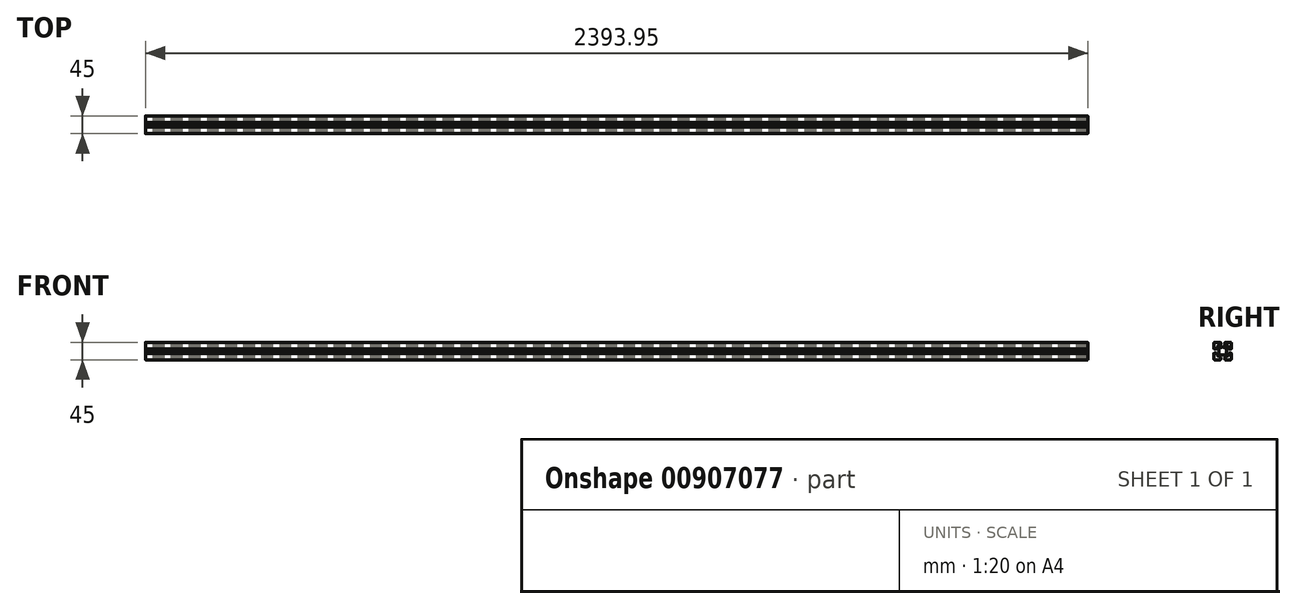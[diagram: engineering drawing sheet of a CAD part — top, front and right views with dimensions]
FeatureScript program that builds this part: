
annotation { "Feature Type Name" : "Feature", "Feature Type Description" : "" }
export const myFeature = defineFeature(function(context is Context, id is Id, definition is map)
    precondition{}
    {
        {
            var Q0;
            Q0=qCreatedBy(makeId("Right.planeOp"),FACE);
            var sketch = newSketch(context, id + "F0", { "sketchPlane" : qUnion([Q0])});
            skLineSegment(sketch, "E0", {"start": v(-20.09, -10.29) * mm, "end": v(-21.29, -10.29) * mm});
            skArc(sketch, "E1", {"start": v(-21.29, -10.29) * mm, "mid": v(-21.5, -10.38) * mm, "end": v(-21.59, -10.59) * mm});
            skLineSegment(sketch, "E2", {"start": v(-21.59, -10.59) * mm, "end": v(-21.59, -23.99) * mm});
            skArc(sketch, "E3", {"start": v(-21.59, -23.99) * mm, "mid": v(-20.7, -26.11) * mm, "end": v(-18.59, -26.99) * mm});
            skLineSegment(sketch, "E4", {"start": v(-18.59, -26.99) * mm, "end": v(-5.19, -26.99) * mm});
            skArc(sketch, "E5", {"start": v(-5.19, -26.99) * mm, "mid": v(-4.98, -26.9) * mm, "end": v(-4.89, -26.69) * mm});
            skLineSegment(sketch, "E6", {"start": v(-4.89, -26.69) * mm, "end": v(-4.89, -25.49) * mm});
            skLineSegment(sketch, "E7", {"start": v(-4.89, -25.49) * mm, "end": v(-4.39, -25.49) * mm});
            skArc(sketch, "E8", {"start": v(-4.39, -25.49) * mm, "mid": v(-4.18, -25.4) * mm, "end": v(-4.09, -25.19) * mm});
            skLineSegment(sketch, "E9", {"start": v(-4.09, -25.19) * mm, "end": v(-4.09, -21.29) * mm});
            skArc(sketch, "E10", {"start": v(-4.09, -21.29) * mm, "mid": v(-4.18, -21.08) * mm, "end": v(-4.39, -20.99) * mm});
            skLineSegment(sketch, "E11", {"start": v(-4.39, -20.99) * mm, "end": v(-9.14, -20.99) * mm});
            skLineSegment(sketch, "E12", {"start": v(-9.14, -20.99) * mm, "end": v(-9.14, -16.88) * mm});
            skLineSegment(sketch, "E13", {"start": v(-9.14, -16.88) * mm, "end": v(-6.25, -13.99) * mm});
            skLineSegment(sketch, "E14", {"start": v(-6.25, -13.99) * mm, "end": v(-2.21, -13.99) * mm});
            skArc(sketch, "E15", {"start": v(-2.21, -13.99) * mm, "mid": v(0.91, -14.49) * mm, "end": v(4.03, -13.99) * mm});
            skLineSegment(sketch, "E16", {"start": v(-20.09, -10.29) * mm, "end": v(-20.09, -9.79) * mm});
            skArc(sketch, "E17", {"start": v(-20.09, -9.79) * mm, "mid": v(-20, -9.58) * mm, "end": v(-19.79, -9.49) * mm});
            skLineSegment(sketch, "E18", {"start": v(-19.79, -9.49) * mm, "end": v(-15.89, -9.49) * mm});
            skArc(sketch, "E19", {"start": v(-15.89, -9.49) * mm, "mid": v(-15.68, -9.58) * mm, "end": v(-15.59, -9.79) * mm});
            skLineSegment(sketch, "E20", {"start": v(-15.59, -9.79) * mm, "end": v(-15.59, -14.54) * mm});
            skLineSegment(sketch, "E21", {"start": v(-15.59, -14.54) * mm, "end": v(-11.48, -14.54) * mm});
            skLineSegment(sketch, "E22", {"start": v(-11.48, -14.54) * mm, "end": v(-8.59, -11.65) * mm});
            skLineSegment(sketch, "E23", {"start": v(-8.59, -11.65) * mm, "end": v(-8.59, -7.61) * mm});
            skLineSegment(sketch, "E24", {"start": v(29.82, -4.49) * mm, "end": v(-31.05, -4.49) * mm});
            skLineSegment(sketch, "E25.MirrorCS", {"start": v(6.71, -25.49) * mm, "end": v(6.21, -25.49) * mm});
            skArc(sketch, "E26.MirrorCS", {"start": v(7.01, -26.99) * mm, "mid": v(6.8, -26.9) * mm, "end": v(6.71, -26.69) * mm});
            skLineSegment(sketch, "E27.MirrorCS", {"start": v(10.41, -11.65) * mm, "end": v(10.41, -7.61) * mm});
            skArc(sketch, "E28.MirrorCS", {"start": v(6.21, -25.49) * mm, "mid": v(6, -25.4) * mm, "end": v(5.91, -25.19) * mm});
            skLineSegment(sketch, "E29.MirrorCS", {"start": v(6.71, -26.69) * mm, "end": v(6.71, -25.49) * mm});
            skArc(sketch, "E30.MirrorCS", {"start": v(5.91, -21.29) * mm, "mid": v(6, -21.08) * mm, "end": v(6.21, -20.99) * mm});
            skLineSegment(sketch, "E31.MirrorCS", {"start": v(10.96, -16.88) * mm, "end": v(8.07, -13.99) * mm});
            skLineSegment(sketch, "E32.MirrorCS", {"start": v(13.3, -14.54) * mm, "end": v(10.41, -11.65) * mm});
            skLineSegment(sketch, "E33.MirrorCS", {"start": v(17.41, -14.54) * mm, "end": v(13.3, -14.54) * mm});
            skLineSegment(sketch, "E34.MirrorCS", {"start": v(17.41, -9.79) * mm, "end": v(17.41, -14.54) * mm});
            skLineSegment(sketch, "E35.MirrorCS", {"start": v(6.21, -20.99) * mm, "end": v(10.96, -20.99) * mm});
            skLineSegment(sketch, "E36.MirrorCS", {"start": v(8.07, -13.99) * mm, "end": v(4.03, -13.99) * mm});
            skArc(sketch, "E37.MirrorCS", {"start": v(4.03, -13.99) * mm, "mid": v(0.91, -14.49) * mm, "end": v(-2.21, -13.99) * mm});
            skLineSegment(sketch, "E38.MirrorCS", {"start": v(10.96, -20.99) * mm, "end": v(10.96, -16.88) * mm});
            skLineSegment(sketch, "E39.MirrorCS", {"start": v(5.91, -25.19) * mm, "end": v(5.91, -21.29) * mm});
            skArc(sketch, "E40.MirrorCS", {"start": v(23.41, -23.99) * mm, "mid": v(22.53, -26.11) * mm, "end": v(20.41, -26.99) * mm});
            skLineSegment(sketch, "E41.MirrorCS", {"start": v(20.41, -26.99) * mm, "end": v(7.01, -26.99) * mm});
            skLineSegment(sketch, "E42.MirrorCS", {"start": v(23.41, -10.59) * mm, "end": v(23.41, -23.99) * mm});
            skArc(sketch, "E43.MirrorCS", {"start": v(17.71, -9.49) * mm, "mid": v(17.5, -9.58) * mm, "end": v(17.41, -9.79) * mm});
            skArc(sketch, "E44.MirrorCS", {"start": v(23.11, -10.29) * mm, "mid": v(23.32, -10.38) * mm, "end": v(23.41, -10.59) * mm});
            skLineSegment(sketch, "E45.MirrorCS", {"start": v(21.91, -10.29) * mm, "end": v(21.91, -9.79) * mm});
            skLineSegment(sketch, "E46.MirrorCS", {"start": v(21.91, -10.29) * mm, "end": v(23.11, -10.29) * mm});
            skArc(sketch, "E47.MirrorCS", {"start": v(21.91, -9.79) * mm, "mid": v(21.82, -9.58) * mm, "end": v(21.61, -9.49) * mm});
            skLineSegment(sketch, "E48.MirrorCS", {"start": v(21.61, -9.49) * mm, "end": v(17.71, -9.49) * mm});
            skLineSegment(sketch, "E49.MirrorCS", {"start": v(6.71, 16.51) * mm, "end": v(6.21, 16.51) * mm});
            skArc(sketch, "E50.MirrorCS", {"start": v(-4.39, 16.51) * mm, "mid": v(-4.18, 16.42) * mm, "end": v(-4.09, 16.21) * mm});
            skLineSegment(sketch, "E51.MirrorCS", {"start": v(-4.89, 16.51) * mm, "end": v(-4.39, 16.51) * mm});
            skArc(sketch, "E52.MirrorCS", {"start": v(5.91, 12.31) * mm, "mid": v(6, 12.1) * mm, "end": v(6.21, 12.01) * mm});
            skLineSegment(sketch, "E53.MirrorCS", {"start": v(6.71, 17.71) * mm, "end": v(6.71, 16.51) * mm});
            skLineSegment(sketch, "E54.MirrorCS", {"start": v(-4.89, 17.71) * mm, "end": v(-4.89, 16.51) * mm});
            skArc(sketch, "E55.MirrorCS", {"start": v(-5.19, 18.01) * mm, "mid": v(-4.98, 17.92) * mm, "end": v(-4.89, 17.71) * mm});
            skArc(sketch, "E56.MirrorCS", {"start": v(-4.09, 12.31) * mm, "mid": v(-4.18, 12.1) * mm, "end": v(-4.39, 12.01) * mm});
            skArc(sketch, "E57.MirrorCS", {"start": v(7.01, 18.01) * mm, "mid": v(6.8, 17.92) * mm, "end": v(6.71, 17.71) * mm});
            skArc(sketch, "E58.MirrorCS", {"start": v(6.21, 16.51) * mm, "mid": v(6, 16.42) * mm, "end": v(5.91, 16.21) * mm});
            skArc(sketch, "E59.MirrorCS", {"start": v(23.11, 1.31) * mm, "mid": v(23.32, 1.4) * mm, "end": v(23.41, 1.61) * mm});
            skLineSegment(sketch, "E60.MirrorCS", {"start": v(21.91, 1.31) * mm, "end": v(21.91, 0.81) * mm});
            skArc(sketch, "E61.MirrorCS", {"start": v(-15.89, 0.51) * mm, "mid": v(-15.68, 0.6) * mm, "end": v(-15.59, 0.81) * mm});
            skArc(sketch, "E62.MirrorCS", {"start": v(-21.29, 1.31) * mm, "mid": v(-21.5, 1.4) * mm, "end": v(-21.59, 1.61) * mm});
            skArc(sketch, "E63.MirrorCS", {"start": v(17.71, 0.51) * mm, "mid": v(17.5, 0.6) * mm, "end": v(17.41, 0.81) * mm});
            skArc(sketch, "E64.MirrorCS", {"start": v(21.91, 0.81) * mm, "mid": v(21.82, 0.6) * mm, "end": v(21.61, 0.51) * mm});
            skLineSegment(sketch, "E65.MirrorCS", {"start": v(21.91, 1.31) * mm, "end": v(23.11, 1.31) * mm});
            skArc(sketch, "E66.MirrorCS", {"start": v(14.31, 5.31) * mm, "mid": v(14.1, 5.4) * mm, "end": v(14.01, 5.61) * mm});
            skArc(sketch, "E67.MirrorCS", {"start": v(-20.09, 0.81) * mm, "mid": v(-20, 0.6) * mm, "end": v(-19.79, 0.51) * mm});
            skLineSegment(sketch, "E68.MirrorCS", {"start": v(-20.09, 1.31) * mm, "end": v(-21.29, 1.31) * mm});
            skLineSegment(sketch, "E69.MirrorCS", {"start": v(-20.09, 1.31) * mm, "end": v(-20.09, 0.81) * mm});
            skLineSegment(sketch, "E70.MirrorCS", {"start": v(8.07, 5.01) * mm, "end": v(4.03, 5.01) * mm});
            skLineSegment(sketch, "E71.MirrorCS", {"start": v(-4.09, 16.21) * mm, "end": v(-4.09, 12.31) * mm});
            skLineSegment(sketch, "E72.MirrorCS", {"start": v(-9.14, 12.01) * mm, "end": v(-9.14, 7.9) * mm});
            skLineSegment(sketch, "E73.MirrorCS", {"start": v(-15.59, 5.56) * mm, "end": v(-11.48, 5.56) * mm});
            skLineSegment(sketch, "E74.MirrorCS", {"start": v(-4.39, 12.01) * mm, "end": v(-9.14, 12.01) * mm});
            skLineSegment(sketch, "E75.MirrorCS", {"start": v(-9.14, 7.9) * mm, "end": v(-6.25, 5.01) * mm});
            skLineSegment(sketch, "E76.MirrorCS", {"start": v(10.96, 12.01) * mm, "end": v(10.96, 7.9) * mm});
            skArc(sketch, "E77.MirrorCS", {"start": v(-21.59, 15.01) * mm, "mid": v(-20.7, 17.13) * mm, "end": v(-18.59, 18.01) * mm});
            skLineSegment(sketch, "E78.MirrorCS", {"start": v(23.41, 1.61) * mm, "end": v(23.41, 15.01) * mm});
            skLineSegment(sketch, "E79.MirrorCS", {"start": v(13.3, 5.56) * mm, "end": v(10.41, 2.67) * mm});
            skLineSegment(sketch, "E80.MirrorCS", {"start": v(-8.59, 2.67) * mm, "end": v(-8.59, -1.37) * mm});
            skLineSegment(sketch, "E81.MirrorCS", {"start": v(-15.59, 0.81) * mm, "end": v(-15.59, 5.56) * mm});
            skLineSegment(sketch, "E82.MirrorCS", {"start": v(10.41, 2.67) * mm, "end": v(10.41, -1.37) * mm});
            skLineSegment(sketch, "E83.MirrorCS", {"start": v(-18.59, 18.01) * mm, "end": v(-5.19, 18.01) * mm});
            skLineSegment(sketch, "E84.MirrorCS", {"start": v(10.96, 7.9) * mm, "end": v(8.07, 5.01) * mm});
            skLineSegment(sketch, "E85.MirrorCS", {"start": v(17.41, 5.56) * mm, "end": v(13.3, 5.56) * mm});
            skArc(sketch, "E86.MirrorCS", {"start": v(23.41, 15.01) * mm, "mid": v(22.53, 17.13) * mm, "end": v(20.41, 18.01) * mm});
            skLineSegment(sketch, "E87.MirrorCS", {"start": v(5.91, 16.21) * mm, "end": v(5.91, 12.31) * mm});
            skLineSegment(sketch, "E88.MirrorCS", {"start": v(17.41, 0.81) * mm, "end": v(17.41, 5.56) * mm});
            skLineSegment(sketch, "E89.MirrorCS", {"start": v(-11.48, 5.56) * mm, "end": v(-8.59, 2.67) * mm});
            skLineSegment(sketch, "E90.MirrorCS", {"start": v(-6.25, 5.01) * mm, "end": v(-2.21, 5.01) * mm});
            skLineSegment(sketch, "E91.MirrorCS", {"start": v(-21.59, 1.61) * mm, "end": v(-21.59, 15.01) * mm});
            skArc(sketch, "E92.MirrorCS", {"start": v(4.03, 5.01) * mm, "mid": v(0.91, 5.51) * mm, "end": v(-2.21, 5.01) * mm});
            skLineSegment(sketch, "E93.MirrorCS", {"start": v(6.21, 12.01) * mm, "end": v(10.96, 12.01) * mm});
            skArc(sketch, "E94.MirrorCS", {"start": v(-2.21, 5.01) * mm, "mid": v(0.91, 5.51) * mm, "end": v(4.03, 5.01) * mm});
            skLineSegment(sketch, "E95.MirrorCS", {"start": v(20.41, 18.01) * mm, "end": v(7.01, 18.01) * mm});
            skLineSegment(sketch, "E96.MirrorCS", {"start": v(-19.79, 0.51) * mm, "end": v(-15.89, 0.51) * mm});
            skLineSegment(sketch, "E97.MirrorCS", {"start": v(21.61, 0.51) * mm, "end": v(17.71, 0.51) * mm});
            skLineSegment(sketch, "E98.MirrorCS", {"start": v(0.91, -27.65) * mm, "end": v(0.91, 19.82) * mm});
            skArc(sketch, "E99", {"start": v(-8.59, -1.37) * mm, "mid": v(-9.09, -4.49) * mm, "end": v(-8.59, -7.61) * mm});
            skArc(sketch, "E100", {"start": v(10.41, -7.61) * mm, "mid": v(10.91, -4.49) * mm, "end": v(10.41, -1.37) * mm});
            skSolve(sketch);
        }
        {
            var Q0;
            Q0 = qSketchRegion(id + "F0", true);
            extrude(context, id + "F1", {"entities" : qUnion([Q0]), "depth" : 2393.95 * mm, "offsetDistance" : 25.4 * mm});
        }
    });
